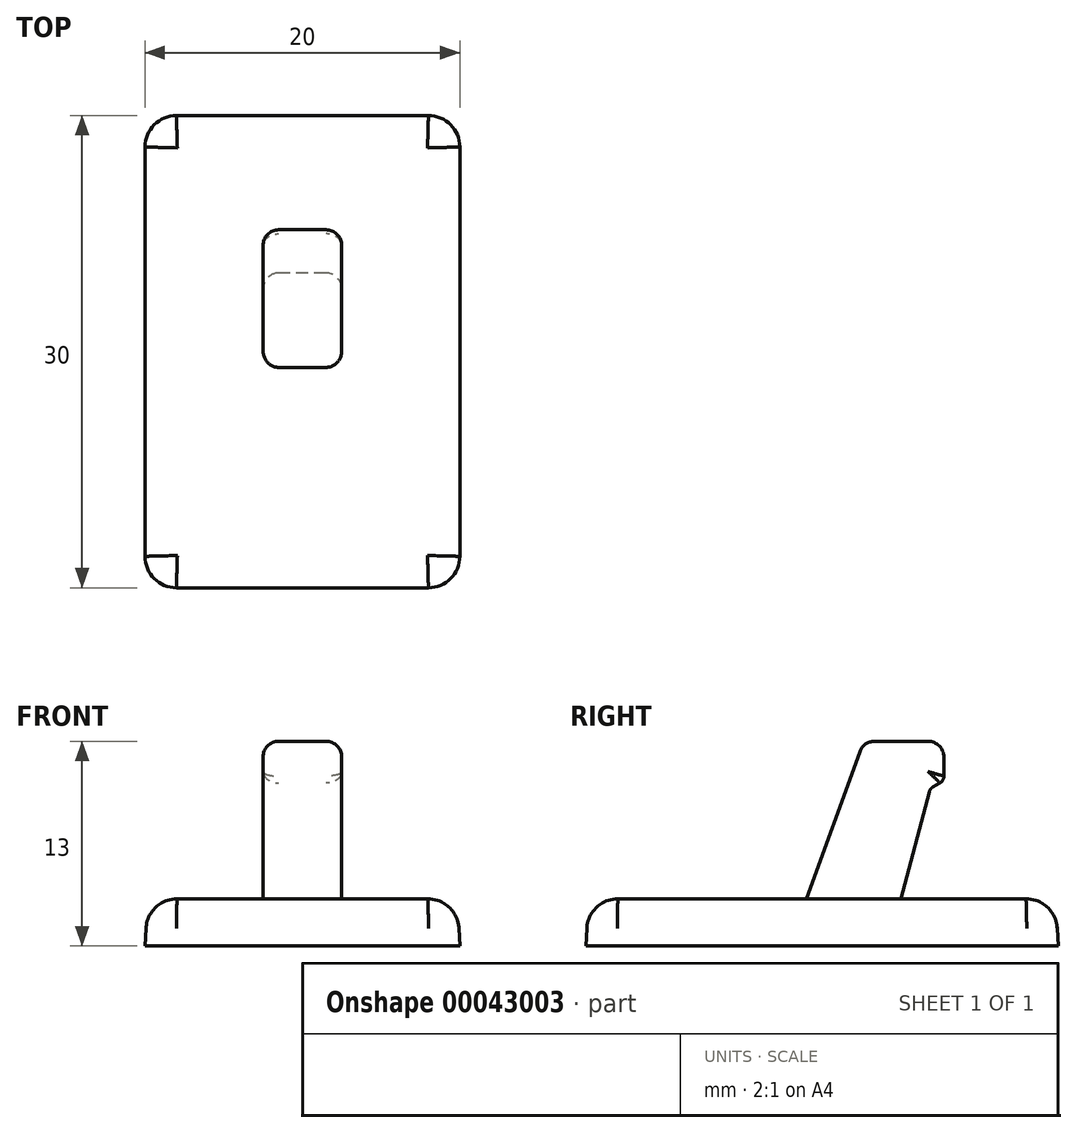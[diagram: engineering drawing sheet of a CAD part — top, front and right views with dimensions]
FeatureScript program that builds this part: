
annotation { "Feature Type Name" : "Feature", "Feature Type Description" : "" }
export const myFeature = defineFeature(function(context is Context, id is Id, definition is map)
    precondition{}
    {
        {
            var Q0;
            Q0=qCreatedBy(makeId("Top.planeOp"),FACE);
            var sketch = newSketch(context, id + "F0", { "sketchPlane" : qUnion([Q0])});
            skLineSegment(sketch, "E0.rect.bottom", {"start": v(8, 15) * mm, "end": v(-8, 15) * mm});
            skLineSegment(sketch, "E0.rect.top", {"start": v(8, -15) * mm, "end": v(-8, -15) * mm});
            skLineSegment(sketch, "E0.rect.left", {"start": v(10, 13) * mm, "end": v(10, -13) * mm});
            skLineSegment(sketch, "E0.rect.right", {"start": v(-10, 13) * mm, "end": v(-10, -13) * mm});
            skPoint(sketch, "E0.rect.middle", {"position": v(0, 0) * mm});
            skPoint(sketch, "E1.visualSharp", {"position": v(-10, -15) * mm});
            skArc(sketch, "E1.filletArc", {"start": v(-10, -13) * mm, "mid": v(-9.41, -14.41) * mm, "end": v(-8, -15) * mm});
            skPoint(sketch, "E2.visualSharp", {"position": v(10, -15) * mm});
            skArc(sketch, "E2.filletArc", {"start": v(8, -15) * mm, "mid": v(9.41, -14.41) * mm, "end": v(10, -13) * mm});
            skPoint(sketch, "E3.visualSharp", {"position": v(10, 15) * mm});
            skArc(sketch, "E3.filletArc", {"start": v(10, 13) * mm, "mid": v(9.41, 14.41) * mm, "end": v(8, 15) * mm});
            skPoint(sketch, "E4.visualSharp", {"position": v(-10, 15) * mm});
            skArc(sketch, "E4.filletArc", {"start": v(-8, 15) * mm, "mid": v(-9.41, 14.41) * mm, "end": v(-10, 13) * mm});
            skSolve(sketch);
        }
        {
            var Q0;
            Q0=makeQuery(id+"F0.imprint","IMPRINT",FACE,{"disambiguationData":[TD([[makeQuery(id+"F0.imprint","IMPRINT",EDGE,{"derivedFrom":sQuery(id+"F0.wireOp",EDGE,"E0.rect.bottom")}),1.0]])]});
            extrude(context, id + "F1", {"entities" : qUnion([Q0]), "depth" : 3 * mm, "hasDraft" : true, "draftAngle" : 3 * degree, "draftPullDirection" : true});
        }
        {
            var Q0;
            Q0=makeQuery(id+"F1.opExtrude","CAP_EDGE",EDGE,{"disambiguationData":[OSD([sQuery(id+"F0.wireOp",EDGE,"E0.rect.bottom")])],"isStart":false});
            fillet(context, id + "F2", {"entities" : qUnion([Q0]), "radius" : 2 * mm, "tangentPropagation" : true, "allowEdgeOverflow" : false});
        }
        {
            var Q0;
            Q0=qCreatedBy(makeId("Right.planeOp"),FACE);
            var sketch = newSketch(context, id + "F3", { "sketchPlane" : qUnion([Q0])});
            skLineSegment(sketch, "E5", {"start": v(6.88, 10) * mm, "end": v(5, 3) * mm});
            skLineSegment(sketch, "E6", {"start": v(6.88, 10) * mm, "end": v(7.74, 10.5) * mm});
            skLineSegment(sketch, "E7", {"start": v(7.74, 10.5) * mm, "end": v(7.74, 12) * mm});
            skLineSegment(sketch, "E8", {"start": v(6.74, 13) * mm, "end": v(3.34, 13) * mm});
            skLineSegment(sketch, "E9", {"start": v(2.4, 12.34) * mm, "end": v(-1, 3) * mm});
            skLineSegment(sketch, "E10", {"start": v(-1, 3) * mm, "end": v(5, 3) * mm});
            skPoint(sketch, "E11.visualSharp", {"position": v(2.64, 13) * mm});
            skArc(sketch, "E11.filletArc", {"start": v(3.34, 13) * mm, "mid": v(2.77, 12.82) * mm, "end": v(2.4, 12.34) * mm});
            skPoint(sketch, "E12.visualSharp", {"position": v(7.74, 13) * mm});
            skArc(sketch, "E12.filletArc", {"start": v(7.74, 12) * mm, "mid": v(7.45, 12.7) * mm, "end": v(6.74, 13) * mm});
            skSolve(sketch);
        }
        {
            var Q0;
            Q0=makeQuery(id+"F3.imprint","IMPRINT",FACE,{"disambiguationData":[TD([[makeQuery(id+"F3.imprint","IMPRINT",EDGE,{"derivedFrom":sQuery(id+"F3.wireOp",EDGE,"E5")}),-1.0]])]});
            extrude(context, id + "F4", {"entities" : qUnion([Q0]), "operationType" : NewBodyOperationType.ADD, "endBound" : BoundingType.SYMMETRIC, "depth" : 5 * mm});
        }
        {
            var Q0;
            Q0=makeQuery(id+"F4.opExtrude","SWEPT_EDGE",EDGE,{"disambiguationData":[OSD([sQuery(id+"F3.wireOp",EDGE,"E5"),sQuery(id+"F3.wireOp",EDGE,"E6")])]});
            var Q1;
            Q1=makeQuery(id+"F4.opExtrude","SWEPT_EDGE",EDGE,{"disambiguationData":[OSD([sQuery(id+"F3.wireOp",EDGE,"E6"),sQuery(id+"F3.wireOp",EDGE,"E7")])]});
            fillet(context, id + "F5", {"entities" : qUnion([Q0, Q1]), "radius" : .5 * mm, "tangentPropagation" : true, "allowEdgeOverflow" : false});
        }
        {
            var Q0;
            Q0=makeQuery(id+"F4.opExtrude","CAP_EDGE",EDGE,{"disambiguationData":[OSD([sQuery(id+"F3.wireOp",EDGE,"E9")])],"isStart":false});
            var Q1;
            Q1=makeQuery(id+"F4.opExtrude","CAP_EDGE",EDGE,{"disambiguationData":[OSD([sQuery(id+"F3.wireOp",EDGE,"E5")])],"isStart":true});
            var Q2;
            Q2=makeQuery(id+"F4.opExtrude","CAP_EDGE",EDGE,{"disambiguationData":[OSD([sQuery(id+"F3.wireOp",EDGE,"E10")])],"isStart":false});
            fillet(context, id + "F6", {"entities" : qUnion([Q0, Q1, Q2]), "radius" : 1 * mm, "tangentPropagation" : true, "allowEdgeOverflow" : false});
        }
    });
